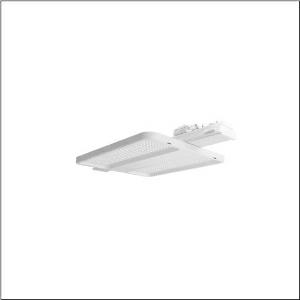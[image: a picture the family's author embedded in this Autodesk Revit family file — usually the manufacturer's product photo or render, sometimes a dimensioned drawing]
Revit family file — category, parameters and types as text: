
# Revit family: highbay_11_fur_licross_tragschiene_midi_51hn11da4fla
name_source: partatom
category: Lighting Fixtures
units: mm (PartAtom-declared; Revit-internal decimal feet)

## family parameters
Cut with Voids When Loaded = No
Host = Face
Light Source = No
Part Type = Normal
Room Calculation Point = No
Round Connector Dimension = Use Diameter
Shared = No

## types (1)
- --- (1 x LED, 15000 lm, 73.2 W, 4000K)
    Apparent Load = 73 VA
    CIE Flux Codes = 85 97 100 100 100
    Color Rendering = 80
    Color Temperature = 4000K
    Default Elevation = 1800 mm
    Description = high bay luminaire Highbay 11 for Licross trunking rail midi; direct symmetric narrow distribution, light control with lens of PMMA; UGR ≤ 22 (X = 4H | Y = 8H | S = 0.25H | reflection values 70/50/20); luminous flux: 15.000lm; light colour: 840, colour temperature: 4000K, MacAdam ≤ 2 SDCM (initial), colour rendering: CRI > 80; luminous efficacy: 204,9lm/W; rated service life: 100.000h (L95) at AT= 25°C; control: DALI 2; luminaire connection: plug, 5-pole, with phase selectionmains connection: 230..240V, AC 50/60Hz; connected load: 73,2W; protection rating (complete): IP64; insulation class (complete): insulation class I (protective earthing); protection symbol: D; impact resistance: IK06; certification: CE, ENEC, VDE, UKCA; internal wiring halogen-free; luminaire LABS conformity tested according to VDMA 24364:2018-05; Suitable for use in the food industry according to the specifications of IFS-Food, HACCP and/or BRC; housing frame of high-performance plastic PA6, matt traffic white (RAL 9016); cover of PMMA; fixing on rail side of steel, galvanised, white; blank cover of PC/ABS, traffic white (RAL 9016); dimension (LxWxH): 750 x 442 x 71mm; permissible operating ambient temperature: -40..+55°C (reducing of maximum allowable ambient temperature of 5°C with ceiling mounting); packaging unit: 1 piece
    Height = 72 mm  [stored 0.23622 ft]
    Lamp = 1 x LED
    Lamp Light Flux = 15000 lm
    Lamp Power = 73.2 W
    Lamp count = 1
    Length = 474 mm
    Luminous efficacy = 205 lm/W
    Manufacturer = Siteco
    ModVariant = No
    Model = 51HN11DA4FLA
    Mounting Place = Ceiling
    Mounting Type = Pendant
    Number of Poles = 1
    OnlyDefault = Yes
    Power Factor = 1
    Product Name = Highbay 11 für Licross Tragschiene midi
    Product group = high bay luminaire
    ProductGroupID = 902
    Protection Class = Protection class I
    Protection Degree = IP 64
    RLX_Detail_Level = 1
    RLX_Emergency_Light_Flux = 0 lm
    RLX_Emergency_Type = 0
    RLX_Emergency_Type_DB = No
    RlxData = <blob elided: 17053 chars, md5=969502a6>
    Socket = socket
    Standby Power = 0 W
    System Light Flux = 15000 lm
    System Power = 73 W
    Type Comments = factory setting: luminous flux: 100 % | dim-lin: 254 | 339 mA
    Type Image = l_1363258.jpg
    URL = http://relux.com
    VarID = @adj_024495
    Voltage = 0 V
    Weight = 0.00 kg
    Width = 442 mm

note: [stored X ft] marks values corroborated as IEEE doubles in the binary element streams (Revit-internal decimal feet)

## geometry (parser evidence)
native form markers: Blend x4, Sweep x12
no freeform markers — native parametric forms only
